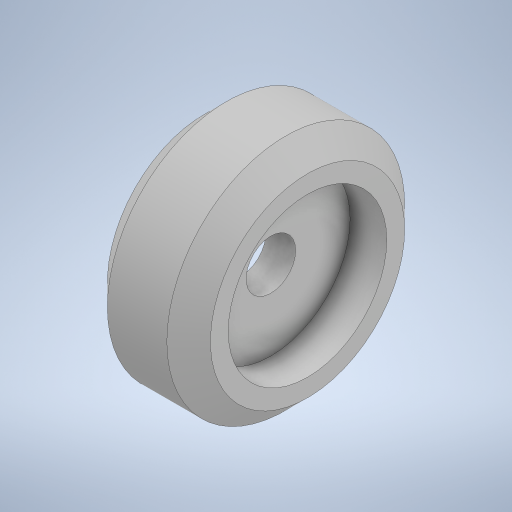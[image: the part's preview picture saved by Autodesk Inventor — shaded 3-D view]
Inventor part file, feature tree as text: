
AUTODESK INVENTOR PART (.ipt)
format: ipt  version: 2024.2 (Build 282272000, 272)  size: 250,368 bytes
history: native  units: in
note: dims shown in document units (in); Inventor stores cm internally (conversion verified against a paired STEP export)
features: extrude x1, sketch x1, other x1
ambient origin geometry x8: Origin, YZ Plane, XZ Plane, XY Plane, X Axis, Y Axis, Z Axis, Center Point
bodies: Solid1 (feature_tree)
feature tree (3):
  extrude  "Extrusion1"  Depth=0.3937in TaperAngle=0.0deg
  sketch  "Sketch1"  dims[d0=0.1969in d1=0.3937in d2=0.0in]
  other  "Corpo1"
